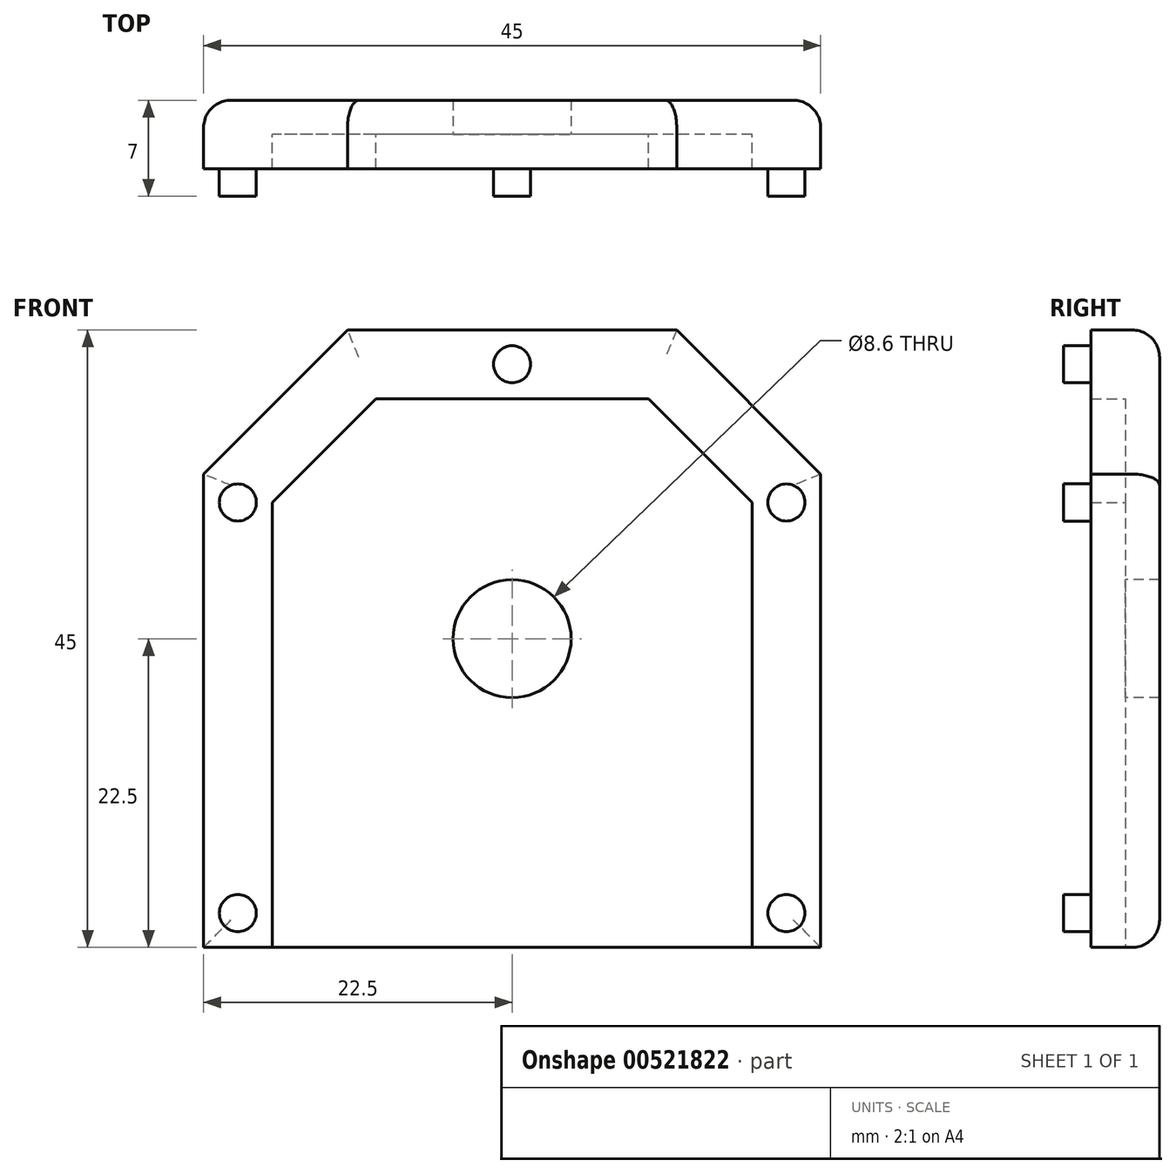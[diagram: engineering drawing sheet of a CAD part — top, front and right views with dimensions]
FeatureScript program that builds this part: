
annotation { "Feature Type Name" : "Feature", "Feature Type Description" : "" }
export const myFeature = defineFeature(function(context is Context, id is Id, definition is map)
    precondition{}
    {
        {
            var Q0;
            Q0=qCreatedBy(makeId("Front.planeOp"),FACE);
            var sketch = newSketch(context, id + "F0", { "sketchPlane" : qUnion([Q0])});
            skLineSegment(sketch, "E0.bottom", {"start": v(22.5, 22.5) * mm, "end": v(-22.5, 22.5) * mm});
            skLineSegment(sketch, "E0.top", {"start": v(22.5, -22.5) * mm, "end": v(-22.5, -22.5) * mm});
            skLineSegment(sketch, "E0.left", {"start": v(22.5, 22.5) * mm, "end": v(22.5, -22.5) * mm});
            skLineSegment(sketch, "E0.right", {"start": v(-22.5, 22.5) * mm, "end": v(-22.5, -22.5) * mm});
            skPoint(sketch, "E0.middle", {"position": v(0, 0) * mm});
            skSolve(sketch);
        }
        {
            var Q0;
            Q0=makeQuery(id+"F0.imprint","IMPRINT",FACE,{"disambiguationData":[TD([[makeQuery(id+"F0.imprint","IMPRINT",EDGE,{"derivedFrom":sQuery(id+"F0.wireOp",EDGE,"E0.bottom")}),1.0]])]});
            extrude(context, id + "F1", {"entities" : qUnion([Q0]), "depth" : 2.5 * mm, "offsetDistance" : 25 * mm});
        }
        {
            var Q0;
            Q0=makeQuery(id+"F1.opExtrude","SWEPT_EDGE",EDGE,{"disambiguationData":[OSD([sQuery(id+"F0.wireOp",EDGE,"E0.bottom"),sQuery(id+"F0.wireOp",EDGE,"E0.right")])]});
            var Q1;
            Q1=makeQuery(id+"F1.opExtrude","SWEPT_EDGE",EDGE,{"disambiguationData":[OSD([sQuery(id+"F0.wireOp",EDGE,"E0.bottom"),sQuery(id+"F0.wireOp",EDGE,"E0.left")])]});
            chamfer(context, id + "F2", {"entities" : qUnion([Q0, Q1]), "width" : 10.5 * mm, "tangentPropagation" : true});
        }
        {
            var Q0;
            Q0=makeQuery(id+"F1.opExtrude","CAP_FACE",FACE,{"disambiguationData":[OSD([sQuery(id+"F0.wireOp",EDGE,"E0.bottom"),sQuery(id+"F0.wireOp",EDGE,"E0.top"),sQuery(id+"F0.wireOp",EDGE,"E0.left"),sQuery(id+"F0.wireOp",EDGE,"E0.right")])],"isStart":false});
            var sketch = newSketch(context, id + "F3", { "sketchPlane" : qUnion([Q0])});
            skLineSegment(sketch, "E1.0", {"start": v(-17.5, 9.93) * mm, "end": v(-17.5, -22.5) * mm});
            skLineSegment(sketch, "E1.1", {"start": v(17.5, 9.93) * mm, "end": v(17.5, -22.5) * mm});
            skLineSegment(sketch, "E1.2", {"start": v(17.5, 9.93) * mm, "end": v(9.93, 17.5) * mm});
            skLineSegment(sketch, "E1.3", {"start": v(9.93, 17.5) * mm, "end": v(-9.93, 17.5) * mm});
            skLineSegment(sketch, "E1.4", {"start": v(-9.93, 17.5) * mm, "end": v(-17.5, 9.93) * mm});
            skCircle(sketch, "E2", {"center": v(0, 0) * mm, "radius": 4.3 * mm});
            skSolve(sketch);
        }
        {
            var Q0;
            {var subQ7=sQuery(id+"F3.wireOp",EDGE,"E1.0");Q0=makeQuery(id+"F3.imprint","IMPRINT",FACE,{"disambiguationData":[TD([[makeQuery(id+"F3.imprint","IMPRINT",EDGE,{"derivedFrom":subQ7}),-1.0]])]});}
            extrude(context, id + "F4", {"entities" : qUnion([Q0]), "operationType" : NewBodyOperationType.ADD, "depth" : 2.5 * mm, "offsetDistance" : 25 * mm});
        }
        {
            var Q0;
            Q0=makeQuery(id+"F1.opExtrude","CAP_FACE",FACE,{"disambiguationData":[OSD([sQuery(id+"F0.wireOp",EDGE,"E0.bottom"),sQuery(id+"F0.wireOp",EDGE,"E0.top"),sQuery(id+"F0.wireOp",EDGE,"E0.left"),sQuery(id+"F0.wireOp",EDGE,"E0.right")])],"isStart":true});
            fillet(context, id + "F5", {"entities" : qUnion([Q0]), "radius" : 2 * mm, "tangentPropagation" : true, "allowEdgeOverflow" : false});
        }
        {
            var Q0;
            Q0=makeQuery(id+"F3.imprint","IMPRINT",FACE,{"disambiguationData":[TD([[makeQuery(id+"F3.imprint","IMPRINT",EDGE,{"derivedFrom":sQuery(id+"F3.wireOp",EDGE,"E2")}),1.0]])]});
            extrude(context, id + "F6", {"entities" : qUnion([Q0]), "operationType" : NewBodyOperationType.REMOVE, "oppositeDirection" : true, "depth" : 25 * mm, "offsetDistance" : 25 * mm});
        }
        {
            var Q0;
            Q0=makeQuery(id+"F4.opExtrude","CAP_FACE",FACE,{"disambiguationData":[OSD([sQuery(id+"F0.wireOp",EDGE,"E0.bottom"),sQuery(id+"F0.wireOp",EDGE,"E0.top"),sQuery(id+"F0.wireOp",EDGE,"E0.left"),sQuery(id+"F0.wireOp",EDGE,"E0.right"),sQuery(id+"F3.wireOp",EDGE,"E1.0"),sQuery(id+"F3.wireOp",EDGE,"E1.1"),sQuery(id+"F3.wireOp",EDGE,"E1.2"),sQuery(id+"F3.wireOp",EDGE,"E1.3"),sQuery(id+"F3.wireOp",EDGE,"E1.4")])],"isStart":false});
            var sketch = newSketch(context, id + "F7", { "sketchPlane" : qUnion([Q0])});
            skLineSegment(sketch, "E3.0", {"start": v(-17.5, 9.93) * mm, "end": v(-17.5, -22.5) * mm});
            skLineSegment(sketch, "E3.1", {"start": v(17.5, 9.93) * mm, "end": v(17.5, -22.5) * mm});
            skLineSegment(sketch, "E3.2", {"start": v(17.5, 9.93) * mm, "end": v(9.93, 17.5) * mm});
            skLineSegment(sketch, "E3.3", {"start": v(9.93, 17.5) * mm, "end": v(-9.93, 17.5) * mm});
            skLineSegment(sketch, "E3.4", {"start": v(-9.93, 17.5) * mm, "end": v(-17.5, 9.93) * mm});
            skLineSegment(sketch, "E4.bottom", {"start": v(-22.5, -22.5) * mm, "end": v(-20, -22.5) * mm});
            skLineSegment(sketch, "E4.top", {"start": v(-22.5, -20) * mm, "end": v(-20, -20) * mm});
            skLineSegment(sketch, "E4.left", {"start": v(-22.5, -22.5) * mm, "end": v(-22.5, -20) * mm});
            skLineSegment(sketch, "E4.right", {"start": v(-20, -22.5) * mm, "end": v(-20, -20) * mm});
            skLineSegment(sketch, "E5.bottom", {"start": v(17.5, -22.5) * mm, "end": v(20, -22.5) * mm});
            skLineSegment(sketch, "E5.top", {"start": v(17.5, -20) * mm, "end": v(20, -20) * mm});
            skLineSegment(sketch, "E5.left", {"start": v(17.5, -22.5) * mm, "end": v(17.5, -20) * mm});
            skLineSegment(sketch, "E5.right", {"start": v(20, -22.5) * mm, "end": v(20, -20) * mm});
            skLineSegment(sketch, "E6.bottom", {"start": v(17.5, 9.93) * mm, "end": v(20, 9.93) * mm});
            skLineSegment(sketch, "E6.top", {"start": v(17.5, 7.43) * mm, "end": v(20, 7.43) * mm});
            skLineSegment(sketch, "E6.left", {"start": v(17.5, 9.93) * mm, "end": v(17.5, 7.43) * mm});
            skLineSegment(sketch, "E6.right", {"start": v(20, 9.93) * mm, "end": v(20, 7.43) * mm});
            skLineSegment(sketch, "E7.bottom", {"start": v(-17.5, 9.93) * mm, "end": v(-20, 9.93) * mm});
            skLineSegment(sketch, "E7.top", {"start": v(-17.5, 7.43) * mm, "end": v(-20, 7.43) * mm});
            skLineSegment(sketch, "E7.left", {"start": v(-17.5, 9.93) * mm, "end": v(-17.5, 7.43) * mm});
            skLineSegment(sketch, "E7.right", {"start": v(-20, 9.93) * mm, "end": v(-20, 7.43) * mm});
            skLineSegment(sketch, "E8", {"start": v(0, 17.5) * mm, "end": v(0, 20) * mm});
            skCircle(sketch, "E9", {"center": v(-20, 9.93) * mm, "radius": 1.35 * mm});
            skCircle(sketch, "E10", {"center": v(-20, -20) * mm, "radius": 1.35 * mm});
            skCircle(sketch, "E11", {"center": v(0, 20) * mm, "radius": 1.35 * mm});
            skCircle(sketch, "E12", {"center": v(20, 9.93) * mm, "radius": 1.35 * mm});
            skCircle(sketch, "E13", {"center": v(20, -20) * mm, "radius": 1.35 * mm});
            skSolve(sketch);
        }
        {
            var Q0;
            {var subQ0=sQuery(id+"F7.wireOp",EDGE,"E7.right");var subQ1=sQuery(id+"F7.wireOp",EDGE,"E7.bottom");var subQ2=makeQuery(id+"F7.imprint","INTERSECT",VERTEX,{"derivedFrom":[subQ1,subQ0]});Q0=makeQuery(id+"F7.imprint","IMPRINT",FACE,{"disambiguationData":[TD([[makeQuery(id+"F7.imprint","IMPRINT",EDGE,{"disambiguationData":[TD([[subQ2,1.0]])],"derivedFrom":subQ1}),1.0]])]});}
            var Q1;
            {var subQ0=sQuery(id+"F7.wireOp",EDGE,"E7.right");var subQ1=sQuery(id+"F7.wireOp",EDGE,"E7.bottom");var subQ2=makeQuery(id+"F7.imprint","INTERSECT",VERTEX,{"derivedFrom":[subQ1,subQ0]});Q1=makeQuery(id+"F7.imprint","IMPRINT",FACE,{"disambiguationData":[TD([[makeQuery(id+"F7.imprint","IMPRINT",EDGE,{"disambiguationData":[TD([[subQ2,1.0]])],"derivedFrom":subQ1}),-1.0]])]});}
            var Q2;
            {var subQ0=sQuery(id+"F7.wireOp",EDGE,"E4.right");var subQ1=sQuery(id+"F7.wireOp",EDGE,"E4.top");var subQ2=makeQuery(id+"F7.imprint","INTERSECT",VERTEX,{"derivedFrom":[subQ1,subQ0]});Q2=makeQuery(id+"F7.imprint","IMPRINT",FACE,{"disambiguationData":[TD([[makeQuery(id+"F7.imprint","IMPRINT",EDGE,{"disambiguationData":[TD([[subQ2,1.0]])],"derivedFrom":subQ1}),-1.0]])]});}
            var Q3;
            {var subQ0=sQuery(id+"F7.wireOp",EDGE,"E4.right");var subQ1=sQuery(id+"F7.wireOp",EDGE,"E4.top");var subQ2=makeQuery(id+"F7.imprint","INTERSECT",VERTEX,{"derivedFrom":[subQ1,subQ0]});Q3=makeQuery(id+"F7.imprint","IMPRINT",FACE,{"disambiguationData":[TD([[makeQuery(id+"F7.imprint","IMPRINT",EDGE,{"disambiguationData":[TD([[subQ2,1.0]])],"derivedFrom":subQ1}),1.0]])]});}
            var Q4;
            {var subQ0=sQuery(id+"F7.wireOp",EDGE,"E5.right");var subQ1=sQuery(id+"F7.wireOp",EDGE,"E5.top");var subQ2=makeQuery(id+"F7.imprint","INTERSECT",VERTEX,{"derivedFrom":[subQ1,subQ0]});Q4=makeQuery(id+"F7.imprint","IMPRINT",FACE,{"disambiguationData":[TD([[makeQuery(id+"F7.imprint","IMPRINT",EDGE,{"disambiguationData":[TD([[subQ2,1.0]])],"derivedFrom":subQ1}),-1.0]])]});}
            var Q5;
            {var subQ0=sQuery(id+"F7.wireOp",EDGE,"E5.right");var subQ1=sQuery(id+"F7.wireOp",EDGE,"E5.top");var subQ2=makeQuery(id+"F7.imprint","INTERSECT",VERTEX,{"derivedFrom":[subQ1,subQ0]});Q5=makeQuery(id+"F7.imprint","IMPRINT",FACE,{"disambiguationData":[TD([[makeQuery(id+"F7.imprint","IMPRINT",EDGE,{"disambiguationData":[TD([[subQ2,1.0]])],"derivedFrom":subQ1}),1.0]])]});}
            var Q6;
            {var subQ0=sQuery(id+"F7.wireOp",EDGE,"E6.right");var subQ1=sQuery(id+"F7.wireOp",EDGE,"E6.bottom");var subQ2=makeQuery(id+"F7.imprint","INTERSECT",VERTEX,{"derivedFrom":[subQ1,subQ0]});Q6=makeQuery(id+"F7.imprint","IMPRINT",FACE,{"disambiguationData":[TD([[makeQuery(id+"F7.imprint","IMPRINT",EDGE,{"disambiguationData":[TD([[subQ2,1.0]])],"derivedFrom":subQ1}),-1.0]])]});}
            var Q7;
            {var subQ0=sQuery(id+"F7.wireOp",EDGE,"E6.right");var subQ1=sQuery(id+"F7.wireOp",EDGE,"E6.bottom");var subQ2=makeQuery(id+"F7.imprint","INTERSECT",VERTEX,{"derivedFrom":[subQ1,subQ0]});Q7=makeQuery(id+"F7.imprint","IMPRINT",FACE,{"disambiguationData":[TD([[makeQuery(id+"F7.imprint","IMPRINT",EDGE,{"disambiguationData":[TD([[subQ2,1.0]])],"derivedFrom":subQ1}),1.0]])]});}
            var Q8;
            Q8=makeQuery(id+"F7.imprint","IMPRINT",FACE,{"disambiguationData":[TD([[makeQuery(id+"F7.imprint","IMPRINT",EDGE,{"derivedFrom":sQuery(id+"F7.wireOp",EDGE,"E11")}),1.0]])]});
            extrude(context, id + "F8", {"entities" : qUnion([Q0, Q1, Q2, Q3, Q4, Q5, Q6, Q7, Q8]), "operationType" : NewBodyOperationType.ADD, "depth" : 2 * mm, "offsetDistance" : 25 * mm});
        }
    });
